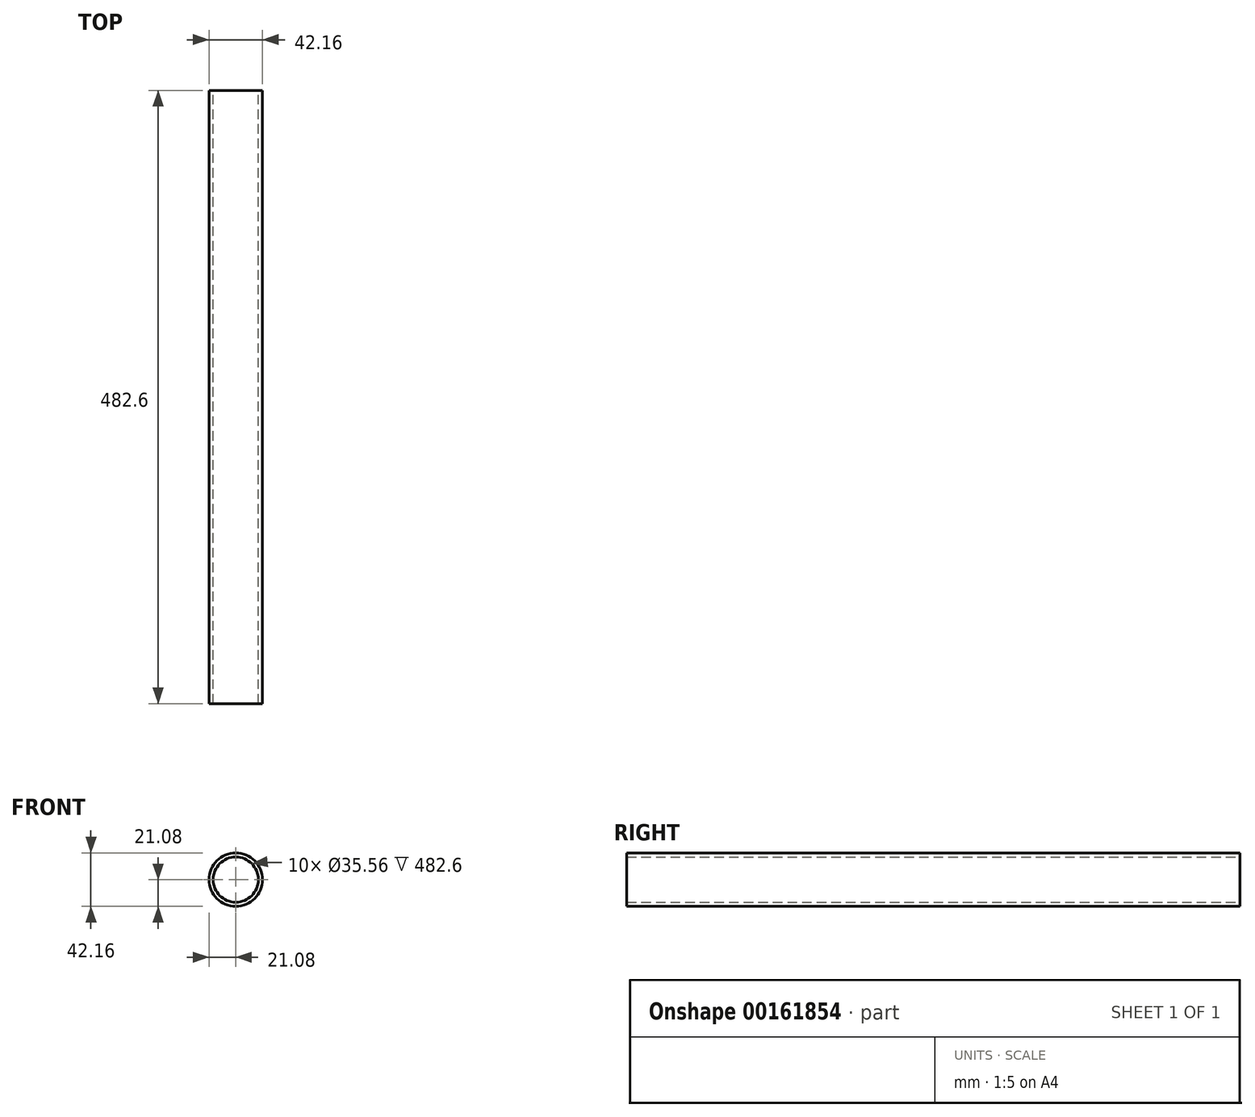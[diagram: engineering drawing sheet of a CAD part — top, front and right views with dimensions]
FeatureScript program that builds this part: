
annotation { "Feature Type Name" : "Feature", "Feature Type Description" : "" }
export const myFeature = defineFeature(function(context is Context, id is Id, definition is map)
    precondition{}
    {
        {
            var Q0;
            Q0=qCreatedBy(makeId("Front.planeOp"),FACE);
            var sketch = newSketch(context, id + "F0", { "sketchPlane" : qUnion([Q0])});
            skCircle(sketch, "E0", {"center": v(0, 0) * mm, "radius": 21.08 * mm});
            skCircle(sketch, "E1", {"center": v(0, 0) * mm, "radius": 17.78 * mm});
            skSolve(sketch);
        }
        {
            var Q0;
            Q0 = qSketchRegion(id + "F0", true);
            extrude(context, id + "F1", {"entities" : qUnion([Q0]), "depth" : 482.6 * mm});
        }
    });
